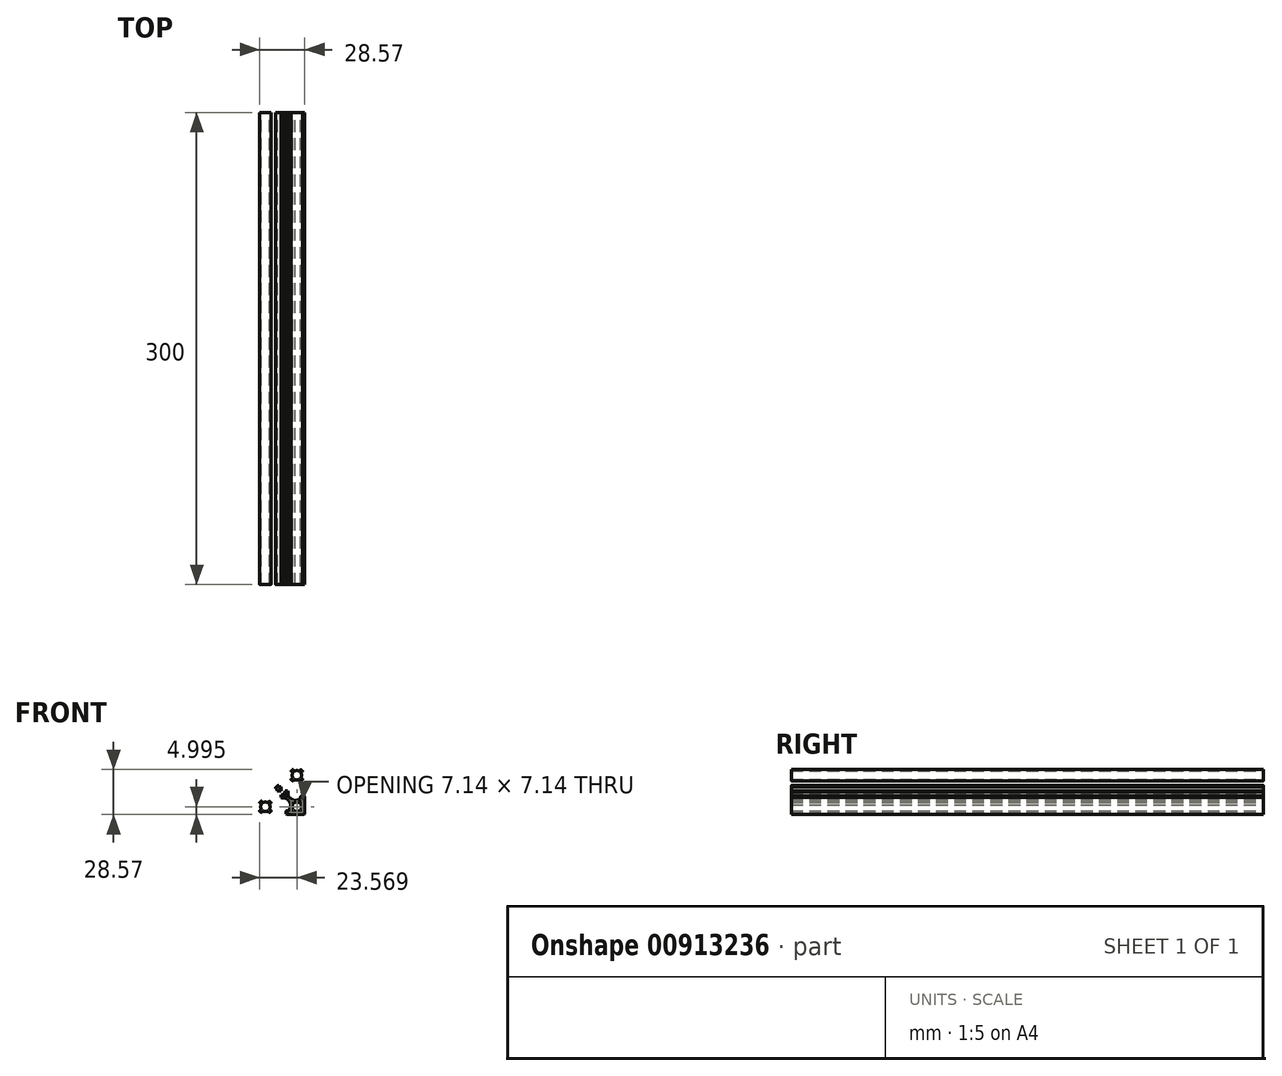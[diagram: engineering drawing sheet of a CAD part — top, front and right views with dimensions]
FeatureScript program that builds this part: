
annotation { "Feature Type Name" : "Feature", "Feature Type Description" : "" }
export const myFeature = defineFeature(function(context is Context, id is Id, definition is map)
    precondition{}
    {
        {
            var Q0;
            Q0=qCreatedBy(makeId("Front.planeOp"),FACE);
            var sketch = newSketch(context, id + "F0", { "sketchPlane" : qUnion([Q0])});
            skLineSegment(sketch, "E0", {"start": v(-2.82, -20.25) * mm, "end": v(-2.82, -15.85) * mm});
            skLineSegment(sketch, "E1", {"start": v(-5.02, -18.05) * mm, "end": v(-0.62, -18.05) * mm});
            skArc(sketch, "E2", {"start": v(-5.5, -19.39) * mm, "mid": v(-5.48, -19.57) * mm, "end": v(-5.56, -19.74) * mm});
            skLineSegment(sketch, "E3", {"start": v(-5.56, -19.74) * mm, "end": v(-6.3, -20.48) * mm});
            skArc(sketch, "E4", {"start": v(-6.3, -20.48) * mm, "mid": v(-6.4, -20.67) * mm, "end": v(-6.32, -20.88) * mm});
            skArc(sketch, "E5", {"start": v(-6.32, -20.88) * mm, "mid": v(-6, -21.24) * mm, "end": v(-5.64, -21.56) * mm});
            skArc(sketch, "E6", {"start": v(-5.64, -21.56) * mm, "mid": v(-5.44, -21.62) * mm, "end": v(-5.24, -21.54) * mm});
            skLineSegment(sketch, "E7", {"start": v(-5.24, -21.54) * mm, "end": v(-4.5, -20.8) * mm});
            skArc(sketch, "E8", {"start": v(-4.5, -20.8) * mm, "mid": v(-4.34, -20.71) * mm, "end": v(-4.16, -20.74) * mm});
            skArc(sketch, "E9", {"start": v(-4.16, -20.74) * mm, "mid": v(-2.82, -21.05) * mm, "end": v(-1.48, -20.74) * mm});
            skArc(sketch, "E10", {"start": v(-1.48, -20.74) * mm, "mid": v(-1.3, -20.71) * mm, "end": v(-1.14, -20.8) * mm});
            skLineSegment(sketch, "E11", {"start": v(-1.14, -20.8) * mm, "end": v(-0.4, -21.54) * mm});
            skArc(sketch, "E12", {"start": v(-0.4, -21.54) * mm, "mid": v(-0.2, -21.62) * mm, "end": v(0, -21.56) * mm});
            skArc(sketch, "E13", {"start": v(0, -21.56) * mm, "mid": v(0.36, -21.24) * mm, "end": v(0.68, -20.88) * mm});
            skArc(sketch, "E14", {"start": v(0.68, -20.88) * mm, "mid": v(0.75, -20.67) * mm, "end": v(0.66, -20.48) * mm});
            skLineSegment(sketch, "E15", {"start": v(0.66, -20.48) * mm, "end": v(-0.08, -19.74) * mm});
            skArc(sketch, "E16", {"start": v(-0.08, -19.74) * mm, "mid": v(-0.16, -19.57) * mm, "end": v(-0.13, -19.39) * mm});
            skArc(sketch, "E17", {"start": v(-0.13, -19.39) * mm, "mid": v(0.18, -18.05) * mm, "end": v(-0.13, -16.72) * mm});
            skArc(sketch, "E18", {"start": v(-0.13, -16.72) * mm, "mid": v(-0.16, -16.54) * mm, "end": v(-0.08, -16.37) * mm});
            skLineSegment(sketch, "E19", {"start": v(-0.08, -16.37) * mm, "end": v(0.66, -15.63) * mm});
            skArc(sketch, "E20", {"start": v(0.66, -15.63) * mm, "mid": v(0.75, -15.44) * mm, "end": v(0.68, -15.23) * mm});
            skArc(sketch, "E21", {"start": v(0.68, -15.23) * mm, "mid": v(0.36, -14.87) * mm, "end": v(0, -14.55) * mm});
            skArc(sketch, "E22", {"start": v(0, -14.55) * mm, "mid": v(-0.2, -14.48) * mm, "end": v(-0.4, -14.57) * mm});
            skLineSegment(sketch, "E23", {"start": v(-0.4, -14.57) * mm, "end": v(-1.14, -15.31) * mm});
            skArc(sketch, "E24", {"start": v(-1.14, -15.31) * mm, "mid": v(-1.3, -15.4) * mm, "end": v(-1.48, -15.37) * mm});
            skArc(sketch, "E25", {"start": v(-1.48, -15.37) * mm, "mid": v(-2.82, -15.05) * mm, "end": v(-4.16, -15.37) * mm});
            skArc(sketch, "E26", {"start": v(-4.16, -15.37) * mm, "mid": v(-4.34, -15.4) * mm, "end": v(-4.5, -15.31) * mm});
            skLineSegment(sketch, "E27", {"start": v(-4.5, -15.31) * mm, "end": v(-5.24, -14.57) * mm});
            skArc(sketch, "E28", {"start": v(-5.24, -14.57) * mm, "mid": v(-5.44, -14.48) * mm, "end": v(-5.64, -14.55) * mm});
            skArc(sketch, "E29", {"start": v(-5.64, -14.55) * mm, "mid": v(-6, -14.87) * mm, "end": v(-6.32, -15.23) * mm});
            skArc(sketch, "E30", {"start": v(-6.32, -15.23) * mm, "mid": v(-6.4, -15.44) * mm, "end": v(-6.3, -15.63) * mm});
            skLineSegment(sketch, "E31", {"start": v(-6.3, -15.63) * mm, "end": v(-5.56, -16.37) * mm});
            skArc(sketch, "E32", {"start": v(-5.56, -16.37) * mm, "mid": v(-5.48, -16.54) * mm, "end": v(-5.5, -16.72) * mm});
            skArc(sketch, "E33", {"start": v(-5.5, -16.72) * mm, "mid": v(-5.82, -18.05) * mm, "end": v(-5.5, -19.39) * mm});
            skLineSegment(sketch, "E34", {"start": v(-5.02, -38.05) * mm, "end": v(-0.62, -38.05) * mm});
            skLineSegment(sketch, "E35", {"start": v(-2.82, -35.85) * mm, "end": v(-2.82, -40.25) * mm});
            skArc(sketch, "E36", {"start": v(-5.5, -36.72) * mm, "mid": v(-5.48, -36.54) * mm, "end": v(-5.56, -36.37) * mm});
            skLineSegment(sketch, "E37", {"start": v(-5.56, -36.37) * mm, "end": v(-6.3, -35.63) * mm});
            skArc(sketch, "E38", {"start": v(-6.3, -35.63) * mm, "mid": v(-6.4, -35.44) * mm, "end": v(-6.33, -35.23) * mm});
            skArc(sketch, "E39", {"start": v(-6.33, -35.23) * mm, "mid": v(-6, -34.87) * mm, "end": v(-5.64, -34.55) * mm});
            skArc(sketch, "E40", {"start": v(-5.64, -34.55) * mm, "mid": v(-5.44, -34.48) * mm, "end": v(-5.24, -34.57) * mm});
            skLineSegment(sketch, "E41", {"start": v(-5.24, -34.57) * mm, "end": v(-4.5, -35.31) * mm});
            skArc(sketch, "E42", {"start": v(-4.5, -35.31) * mm, "mid": v(-4.34, -35.4) * mm, "end": v(-4.16, -35.37) * mm});
            skArc(sketch, "E43", {"start": v(-4.16, -35.37) * mm, "mid": v(-2.82, -35.05) * mm, "end": v(-1.48, -35.37) * mm});
            skArc(sketch, "E44", {"start": v(-1.48, -35.37) * mm, "mid": v(-1.3, -35.4) * mm, "end": v(-1.14, -35.31) * mm});
            skLineSegment(sketch, "E45", {"start": v(-1.14, -35.31) * mm, "end": v(-0.4, -34.57) * mm});
            skArc(sketch, "E46", {"start": v(-0.4, -34.57) * mm, "mid": v(-0.2, -34.48) * mm, "end": v(0, -34.55) * mm});
            skArc(sketch, "E47", {"start": v(0, -34.55) * mm, "mid": v(0.36, -34.87) * mm, "end": v(0.68, -35.23) * mm});
            skArc(sketch, "E48", {"start": v(0.68, -35.23) * mm, "mid": v(0.75, -35.44) * mm, "end": v(0.66, -35.63) * mm});
            skLineSegment(sketch, "E49", {"start": v(0.66, -35.63) * mm, "end": v(-0.08, -36.37) * mm});
            skArc(sketch, "E50", {"start": v(-0.08, -36.37) * mm, "mid": v(-0.16, -36.54) * mm, "end": v(-0.13, -36.72) * mm});
            skArc(sketch, "E51", {"start": v(-0.13, -36.72) * mm, "mid": v(0.18, -38.05) * mm, "end": v(-0.14, -39.4) * mm});
            skArc(sketch, "E52", {"start": v(-0.14, -39.4) * mm, "mid": v(-0.16, -39.57) * mm, "end": v(-0.08, -39.74) * mm});
            skLineSegment(sketch, "E53", {"start": v(-0.08, -39.74) * mm, "end": v(0.66, -40.48) * mm});
            skArc(sketch, "E54", {"start": v(0.66, -40.48) * mm, "mid": v(0.75, -40.67) * mm, "end": v(0.68, -40.88) * mm});
            skArc(sketch, "E55", {"start": v(0.68, -40.88) * mm, "mid": v(0.36, -41.24) * mm, "end": v(0, -41.56) * mm});
            skArc(sketch, "E56", {"start": v(0, -41.56) * mm, "mid": v(-0.2, -41.63) * mm, "end": v(-0.4, -41.54) * mm});
            skLineSegment(sketch, "E57", {"start": v(-0.4, -41.54) * mm, "end": v(-1.14, -40.8) * mm});
            skArc(sketch, "E58", {"start": v(-1.14, -40.8) * mm, "mid": v(-1.3, -40.71) * mm, "end": v(-1.49, -40.74) * mm});
            skArc(sketch, "E59", {"start": v(-1.49, -40.74) * mm, "mid": v(-2.82, -41.05) * mm, "end": v(-4.16, -40.74) * mm});
            skArc(sketch, "E60", {"start": v(-4.16, -40.74) * mm, "mid": v(-4.34, -40.71) * mm, "end": v(-4.5, -40.8) * mm});
            skLineSegment(sketch, "E61", {"start": v(-4.5, -40.8) * mm, "end": v(-5.24, -41.54) * mm});
            skArc(sketch, "E62", {"start": v(-5.24, -41.54) * mm, "mid": v(-5.44, -41.62) * mm, "end": v(-5.64, -41.56) * mm});
            skArc(sketch, "E63", {"start": v(-5.64, -41.56) * mm, "mid": v(-6, -41.24) * mm, "end": v(-6.33, -40.88) * mm});
            skArc(sketch, "E64", {"start": v(-6.33, -40.88) * mm, "mid": v(-6.4, -40.67) * mm, "end": v(-6.3, -40.48) * mm});
            skLineSegment(sketch, "E65", {"start": v(-6.3, -40.48) * mm, "end": v(-5.56, -39.74) * mm});
            skArc(sketch, "E66", {"start": v(-5.56, -39.74) * mm, "mid": v(-5.48, -39.57) * mm, "end": v(-5.5, -39.4) * mm});
            skArc(sketch, "E67", {"start": v(-5.5, -39.4) * mm, "mid": v(-5.82, -38.05) * mm, "end": v(-5.5, -36.72) * mm});
            skArc(sketch, "E68", {"start": v(-20.13, -36.72) * mm, "mid": v(-20.16, -36.54) * mm, "end": v(-20.07, -36.37) * mm});
            skLineSegment(sketch, "E69", {"start": v(-20.07, -36.37) * mm, "end": v(-19.33, -35.63) * mm});
            skArc(sketch, "E70", {"start": v(-19.33, -35.63) * mm, "mid": v(-19.25, -35.44) * mm, "end": v(-19.31, -35.23) * mm});
            skArc(sketch, "E71", {"start": v(-19.31, -35.23) * mm, "mid": v(-19.64, -34.87) * mm, "end": v(-20, -34.55) * mm});
            skArc(sketch, "E72", {"start": v(-20, -34.55) * mm, "mid": v(-20.2, -34.48) * mm, "end": v(-20.4, -34.57) * mm});
            skLineSegment(sketch, "E73", {"start": v(-20.4, -34.57) * mm, "end": v(-21.14, -35.31) * mm});
            skArc(sketch, "E74", {"start": v(-21.14, -35.31) * mm, "mid": v(-21.3, -35.4) * mm, "end": v(-21.48, -35.37) * mm});
            skArc(sketch, "E75", {"start": v(-21.48, -35.37) * mm, "mid": v(-22.82, -35.05) * mm, "end": v(-24.15, -35.37) * mm});
            skArc(sketch, "E76", {"start": v(-24.15, -35.37) * mm, "mid": v(-24.34, -35.4) * mm, "end": v(-24.5, -35.31) * mm});
            skLineSegment(sketch, "E77", {"start": v(-24.5, -35.31) * mm, "end": v(-25.24, -34.57) * mm});
            skArc(sketch, "E78", {"start": v(-25.24, -34.57) * mm, "mid": v(-25.44, -34.48) * mm, "end": v(-25.64, -34.55) * mm});
            skArc(sketch, "E79", {"start": v(-25.64, -34.55) * mm, "mid": v(-26, -34.87) * mm, "end": v(-26.32, -35.23) * mm});
            skArc(sketch, "E80", {"start": v(-26.32, -35.23) * mm, "mid": v(-26.39, -35.44) * mm, "end": v(-26.3, -35.63) * mm});
            skLineSegment(sketch, "E81", {"start": v(-26.3, -35.63) * mm, "end": v(-25.56, -36.37) * mm});
            skArc(sketch, "E82", {"start": v(-25.56, -36.37) * mm, "mid": v(-25.48, -36.54) * mm, "end": v(-25.5, -36.72) * mm});
            skArc(sketch, "E83", {"start": v(-25.5, -36.72) * mm, "mid": v(-25.82, -38.05) * mm, "end": v(-25.5, -39.4) * mm});
            skArc(sketch, "E84", {"start": v(-25.5, -39.4) * mm, "mid": v(-25.48, -39.57) * mm, "end": v(-25.56, -39.74) * mm});
            skLineSegment(sketch, "E85", {"start": v(-25.56, -39.74) * mm, "end": v(-26.3, -40.48) * mm});
            skArc(sketch, "E86", {"start": v(-26.3, -40.48) * mm, "mid": v(-26.39, -40.67) * mm, "end": v(-26.32, -40.88) * mm});
            skArc(sketch, "E87", {"start": v(-26.32, -40.88) * mm, "mid": v(-26, -41.24) * mm, "end": v(-25.64, -41.56) * mm});
            skArc(sketch, "E88", {"start": v(-25.64, -41.56) * mm, "mid": v(-25.44, -41.63) * mm, "end": v(-25.24, -41.54) * mm});
            skLineSegment(sketch, "E89", {"start": v(-25.24, -41.54) * mm, "end": v(-24.5, -40.8) * mm});
            skArc(sketch, "E90", {"start": v(-24.5, -40.8) * mm, "mid": v(-24.33, -40.71) * mm, "end": v(-24.15, -40.74) * mm});
            skArc(sketch, "E91", {"start": v(-24.15, -40.74) * mm, "mid": v(-22.82, -41.05) * mm, "end": v(-21.48, -40.74) * mm});
            skArc(sketch, "E92", {"start": v(-21.48, -40.74) * mm, "mid": v(-21.3, -40.71) * mm, "end": v(-21.14, -40.8) * mm});
            skLineSegment(sketch, "E93", {"start": v(-21.14, -40.8) * mm, "end": v(-20.4, -41.54) * mm});
            skArc(sketch, "E94", {"start": v(-20.4, -41.54) * mm, "mid": v(-20.2, -41.62) * mm, "end": v(-20, -41.56) * mm});
            skArc(sketch, "E95", {"start": v(-20, -41.56) * mm, "mid": v(-19.63, -41.24) * mm, "end": v(-19.31, -40.88) * mm});
            skArc(sketch, "E96", {"start": v(-19.31, -40.88) * mm, "mid": v(-19.25, -40.67) * mm, "end": v(-19.33, -40.48) * mm});
            skLineSegment(sketch, "E97", {"start": v(-19.33, -40.48) * mm, "end": v(-20.07, -39.74) * mm});
            skArc(sketch, "E98", {"start": v(-20.07, -39.74) * mm, "mid": v(-20.16, -39.57) * mm, "end": v(-20.13, -39.4) * mm});
            skArc(sketch, "E99", {"start": v(-20.13, -39.4) * mm, "mid": v(-19.82, -38.05) * mm, "end": v(-20.13, -36.72) * mm});
            skLineSegment(sketch, "E100", {"start": v(-22.82, -35.85) * mm, "end": v(-22.82, -40.25) * mm});
            skLineSegment(sketch, "E101", {"start": v(-20.62, -38.05) * mm, "end": v(-25.02, -38.05) * mm});
            skLineSegment(sketch, "E102", {"start": v(-20.62, -18.05) * mm, "end": v(-25.02, -18.05) * mm});
            skLineSegment(sketch, "E103", {"start": v(-22.82, -20.25) * mm, "end": v(-22.82, -15.85) * mm});
            skLineSegment(sketch, "E104", {"start": v(2.64, -28.05) * mm, "end": v(-29.04, -28.05) * mm});
            skLineSegment(sketch, "E105", {"start": v(-12.82, -44) * mm, "end": v(-12.82, -12.06) * mm});
            skArc(sketch, "E106", {"start": v(-9.58, -26.47) * mm, "mid": v(-9.36, -26.3) * mm, "end": v(-9.38, -26.02) * mm});
            skArc(sketch, "E107", {"start": v(-9.38, -26.02) * mm, "mid": v(-10, -25.23) * mm, "end": v(-10.78, -24.61) * mm});
            skArc(sketch, "E108", {"start": v(-10.78, -24.61) * mm, "mid": v(-11.06, -24.6) * mm, "end": v(-11.23, -24.82) * mm});
            skLineSegment(sketch, "E109", {"start": v(-11.23, -24.82) * mm, "end": v(-11.37, -25.56) * mm});
            skArc(sketch, "E110", {"start": v(-11.37, -25.56) * mm, "mid": v(-11.52, -25.77) * mm, "end": v(-11.78, -25.78) * mm});
            skArc(sketch, "E111", {"start": v(-11.78, -25.78) * mm, "mid": v(-12.82, -25.55) * mm, "end": v(-13.85, -25.78) * mm});
            skArc(sketch, "E112", {"start": v(-13.85, -25.78) * mm, "mid": v(-14.11, -25.77) * mm, "end": v(-14.27, -25.56) * mm});
            skLineSegment(sketch, "E113", {"start": v(-14.27, -25.56) * mm, "end": v(-14.4, -24.82) * mm});
            skArc(sketch, "E114", {"start": v(-14.4, -24.82) * mm, "mid": v(-14.57, -24.6) * mm, "end": v(-14.85, -24.61) * mm});
            skArc(sketch, "E115", {"start": v(-14.85, -24.61) * mm, "mid": v(-15.65, -25.23) * mm, "end": v(-16.26, -26.02) * mm});
            skArc(sketch, "E116", {"start": v(-16.26, -26.02) * mm, "mid": v(-16.27, -26.3) * mm, "end": v(-16.06, -26.47) * mm});
            skLineSegment(sketch, "E117", {"start": v(-16.06, -26.47) * mm, "end": v(-15.31, -26.6) * mm});
            skArc(sketch, "E118", {"start": v(-15.31, -26.6) * mm, "mid": v(-15.1, -26.76) * mm, "end": v(-15.1, -27.02) * mm});
            skArc(sketch, "E119", {"start": v(-15.1, -27.02) * mm, "mid": v(-15.32, -28.05) * mm, "end": v(-15.1, -29.09) * mm});
            skArc(sketch, "E120", {"start": v(-15.1, -29.09) * mm, "mid": v(-15.1, -29.35) * mm, "end": v(-15.31, -29.5) * mm});
            skLineSegment(sketch, "E121", {"start": v(-15.31, -29.5) * mm, "end": v(-16.06, -29.64) * mm});
            skArc(sketch, "E122", {"start": v(-16.06, -29.64) * mm, "mid": v(-16.27, -29.81) * mm, "end": v(-16.26, -30.09) * mm});
            skArc(sketch, "E123", {"start": v(-16.26, -30.09) * mm, "mid": v(-15.65, -30.88) * mm, "end": v(-14.85, -31.5) * mm});
            skArc(sketch, "E124", {"start": v(-14.85, -31.5) * mm, "mid": v(-14.57, -31.51) * mm, "end": v(-14.4, -31.3) * mm});
            skLineSegment(sketch, "E125", {"start": v(-14.4, -31.3) * mm, "end": v(-14.27, -30.55) * mm});
            skArc(sketch, "E126", {"start": v(-14.27, -30.55) * mm, "mid": v(-14.11, -30.34) * mm, "end": v(-13.85, -30.33) * mm});
            skArc(sketch, "E127", {"start": v(-13.85, -30.33) * mm, "mid": v(-12.82, -30.55) * mm, "end": v(-11.78, -30.33) * mm});
            skArc(sketch, "E128", {"start": v(-11.78, -30.33) * mm, "mid": v(-11.52, -30.34) * mm, "end": v(-11.37, -30.55) * mm});
            skLineSegment(sketch, "E129", {"start": v(-11.37, -30.55) * mm, "end": v(-11.23, -31.3) * mm});
            skArc(sketch, "E130", {"start": v(-11.23, -31.3) * mm, "mid": v(-11.06, -31.51) * mm, "end": v(-10.78, -31.5) * mm});
            skArc(sketch, "E131", {"start": v(-10.78, -31.5) * mm, "mid": v(-10, -30.88) * mm, "end": v(-9.38, -30.09) * mm});
            skArc(sketch, "E132", {"start": v(-9.38, -30.09) * mm, "mid": v(-9.36, -29.81) * mm, "end": v(-9.58, -29.64) * mm});
            skLineSegment(sketch, "E133", {"start": v(-9.58, -29.64) * mm, "end": v(-10.32, -29.5) * mm});
            skArc(sketch, "E134", {"start": v(-10.32, -29.5) * mm, "mid": v(-10.53, -29.35) * mm, "end": v(-10.54, -29.09) * mm});
            skArc(sketch, "E135", {"start": v(-10.54, -29.09) * mm, "mid": v(-10.32, -28.05) * mm, "end": v(-10.54, -27.02) * mm});
            skArc(sketch, "E136", {"start": v(-10.54, -27.02) * mm, "mid": v(-10.53, -26.76) * mm, "end": v(-10.32, -26.6) * mm});
            skLineSegment(sketch, "E137", {"start": v(-10.32, -26.6) * mm, "end": v(-9.58, -26.47) * mm});
            skArc(sketch, "E138", {"start": v(-20.13, -19.39) * mm, "mid": v(-20.16, -19.57) * mm, "end": v(-20.08, -19.74) * mm});
            skLineSegment(sketch, "E139", {"start": v(-20.08, -19.74) * mm, "end": v(-19.33, -20.48) * mm});
            skArc(sketch, "E140", {"start": v(-19.33, -20.48) * mm, "mid": v(-19.25, -20.67) * mm, "end": v(-19.31, -20.88) * mm});
            skArc(sketch, "E141", {"start": v(-19.31, -20.88) * mm, "mid": v(-19.64, -21.24) * mm, "end": v(-20, -21.56) * mm});
            skArc(sketch, "E142", {"start": v(-20, -21.56) * mm, "mid": v(-20.2, -21.62) * mm, "end": v(-20.4, -21.54) * mm});
            skLineSegment(sketch, "E143", {"start": v(-20.4, -21.54) * mm, "end": v(-21.14, -20.8) * mm});
            skArc(sketch, "E144", {"start": v(-21.14, -20.8) * mm, "mid": v(-21.3, -20.71) * mm, "end": v(-21.48, -20.74) * mm});
            skArc(sketch, "E145", {"start": v(-21.48, -20.74) * mm, "mid": v(-22.82, -21.05) * mm, "end": v(-24.15, -20.74) * mm});
            skArc(sketch, "E146", {"start": v(-24.15, -20.74) * mm, "mid": v(-24.34, -20.71) * mm, "end": v(-24.5, -20.8) * mm});
            skLineSegment(sketch, "E147", {"start": v(-24.5, -20.8) * mm, "end": v(-25.24, -21.54) * mm});
            skArc(sketch, "E148", {"start": v(-25.24, -21.54) * mm, "mid": v(-25.44, -21.62) * mm, "end": v(-25.64, -21.56) * mm});
            skArc(sketch, "E149", {"start": v(-25.64, -21.56) * mm, "mid": v(-26, -21.24) * mm, "end": v(-26.32, -20.88) * mm});
            skArc(sketch, "E150", {"start": v(-26.32, -20.88) * mm, "mid": v(-26.39, -20.67) * mm, "end": v(-26.3, -20.48) * mm});
            skLineSegment(sketch, "E151", {"start": v(-26.3, -20.48) * mm, "end": v(-25.56, -19.74) * mm});
            skArc(sketch, "E152", {"start": v(-25.56, -19.74) * mm, "mid": v(-25.48, -19.57) * mm, "end": v(-25.5, -19.39) * mm});
            skArc(sketch, "E153", {"start": v(-25.5, -19.39) * mm, "mid": v(-25.82, -18.05) * mm, "end": v(-25.5, -16.72) * mm});
            skArc(sketch, "E154", {"start": v(-25.5, -16.72) * mm, "mid": v(-25.48, -16.54) * mm, "end": v(-25.56, -16.37) * mm});
            skLineSegment(sketch, "E155", {"start": v(-25.56, -16.37) * mm, "end": v(-26.3, -15.63) * mm});
            skArc(sketch, "E156", {"start": v(-26.3, -15.63) * mm, "mid": v(-26.39, -15.44) * mm, "end": v(-26.32, -15.23) * mm});
            skArc(sketch, "E157", {"start": v(-26.32, -15.23) * mm, "mid": v(-26, -14.87) * mm, "end": v(-25.64, -14.55) * mm});
            skArc(sketch, "E158", {"start": v(-25.64, -14.55) * mm, "mid": v(-25.44, -14.48) * mm, "end": v(-25.24, -14.57) * mm});
            skLineSegment(sketch, "E159", {"start": v(-25.24, -14.57) * mm, "end": v(-24.5, -15.31) * mm});
            skArc(sketch, "E160", {"start": v(-24.5, -15.31) * mm, "mid": v(-24.34, -15.4) * mm, "end": v(-24.15, -15.37) * mm});
            skArc(sketch, "E161", {"start": v(-24.15, -15.37) * mm, "mid": v(-22.82, -15.05) * mm, "end": v(-21.48, -15.37) * mm});
            skArc(sketch, "E162", {"start": v(-21.48, -15.37) * mm, "mid": v(-21.3, -15.4) * mm, "end": v(-21.14, -15.31) * mm});
            skLineSegment(sketch, "E163", {"start": v(-21.14, -15.31) * mm, "end": v(-20.4, -14.57) * mm});
            skArc(sketch, "E164", {"start": v(-20.4, -14.57) * mm, "mid": v(-20.2, -14.48) * mm, "end": v(-20, -14.55) * mm});
            skArc(sketch, "E165", {"start": v(-20, -14.55) * mm, "mid": v(-19.64, -14.87) * mm, "end": v(-19.31, -15.23) * mm});
            skArc(sketch, "E166", {"start": v(-19.31, -15.23) * mm, "mid": v(-19.25, -15.44) * mm, "end": v(-19.33, -15.63) * mm});
            skLineSegment(sketch, "E167", {"start": v(-19.33, -15.63) * mm, "end": v(-20.08, -16.37) * mm});
            skArc(sketch, "E168", {"start": v(-20.08, -16.37) * mm, "mid": v(-20.16, -16.54) * mm, "end": v(-20.13, -16.72) * mm});
            skArc(sketch, "E169", {"start": v(-20.13, -16.72) * mm, "mid": v(-19.82, -18.05) * mm, "end": v(-20.13, -19.39) * mm});
            skLineSegment(sketch, "E170", {"start": v(-8.87, -43.05) * mm, "end": v(-9.67, -42.55) * mm});
            skLineSegment(sketch, "E171", {"start": v(-9.67, -42.55) * mm, "end": v(-9.67, -40.85) * mm});
            skArc(sketch, "E172", {"start": v(-9.67, -40.85) * mm, "mid": v(-9.58, -40.64) * mm, "end": v(-9.37, -40.55) * mm});
            skLineSegment(sketch, "E173", {"start": v(-9.37, -40.55) * mm, "end": v(-7.72, -40.55) * mm});
            skLineSegment(sketch, "E174", {"start": v(-7.72, -40.55) * mm, "end": v(-6.73, -37.5) * mm});
            skArc(sketch, "E175", {"start": v(-6.73, -37.5) * mm, "mid": v(-6.68, -37.24) * mm, "end": v(-6.7, -36.98) * mm});
            skArc(sketch, "E176", {"start": v(-6.7, -36.98) * mm, "mid": v(-7.54, -34.94) * mm, "end": v(-8.81, -33.14) * mm});
            skArc(sketch, "E177", {"start": v(-8.81, -33.14) * mm, "mid": v(-9.66, -32.7) * mm, "end": v(-10.6, -32.55) * mm});
            skLineSegment(sketch, "E178", {"start": v(-10.6, -32.55) * mm, "end": v(-12.32, -32.55) * mm});
            skLineSegment(sketch, "E179", {"start": v(-12.32, -32.55) * mm, "end": v(-12.82, -32.05) * mm});
            skLineSegment(sketch, "E180", {"start": v(-12.82, -32.05) * mm, "end": v(-13.32, -32.55) * mm});
            skLineSegment(sketch, "E181", {"start": v(-13.32, -32.55) * mm, "end": v(-15.04, -32.55) * mm});
            skArc(sketch, "E182", {"start": v(-15.04, -32.55) * mm, "mid": v(-15.98, -32.7) * mm, "end": v(-16.82, -33.14) * mm});
            skArc(sketch, "E183", {"start": v(-16.82, -33.14) * mm, "mid": v(-18.1, -34.94) * mm, "end": v(-18.93, -36.98) * mm});
            skArc(sketch, "E184", {"start": v(-18.93, -36.98) * mm, "mid": v(-18.95, -37.24) * mm, "end": v(-18.9, -37.5) * mm});
            skLineSegment(sketch, "E185", {"start": v(-18.9, -37.5) * mm, "end": v(-17.92, -40.55) * mm});
            skLineSegment(sketch, "E186", {"start": v(-17.92, -40.55) * mm, "end": v(-16.27, -40.55) * mm});
            skArc(sketch, "E187", {"start": v(-16.27, -40.55) * mm, "mid": v(-16.06, -40.64) * mm, "end": v(-15.97, -40.85) * mm});
            skLineSegment(sketch, "E188", {"start": v(-15.97, -40.85) * mm, "end": v(-15.97, -42.55) * mm});
            skLineSegment(sketch, "E189", {"start": v(-15.97, -42.55) * mm, "end": v(-16.77, -43.05) * mm});
            skLineSegment(sketch, "E190", {"start": v(-16.77, -43.05) * mm, "end": v(-26.82, -43.05) * mm});
            skArc(sketch, "E191", {"start": v(-26.82, -43.05) * mm, "mid": v(-27.52, -42.76) * mm, "end": v(-27.82, -42.05) * mm});
            skLineSegment(sketch, "E192", {"start": v(-27.82, -42.05) * mm, "end": v(-27.82, -32) * mm});
            skLineSegment(sketch, "E193", {"start": v(-27.82, -32) * mm, "end": v(-27.32, -31.2) * mm});
            skLineSegment(sketch, "E194", {"start": v(-27.32, -31.2) * mm, "end": v(-25.62, -31.2) * mm});
            skArc(sketch, "E195", {"start": v(-25.62, -31.2) * mm, "mid": v(-25.4, -31.3) * mm, "end": v(-25.32, -31.5) * mm});
            skLineSegment(sketch, "E196", {"start": v(-25.32, -31.5) * mm, "end": v(-25.32, -33.15) * mm});
            skLineSegment(sketch, "E197", {"start": v(-25.32, -33.15) * mm, "end": v(-22.27, -34.14) * mm});
            skArc(sketch, "E198", {"start": v(-22.27, -34.14) * mm, "mid": v(-22, -34.19) * mm, "end": v(-21.75, -34.17) * mm});
            skArc(sketch, "E199", {"start": v(-21.75, -34.17) * mm, "mid": v(-19.7, -33.33) * mm, "end": v(-17.9, -32.06) * mm});
            skArc(sketch, "E200", {"start": v(-17.9, -32.06) * mm, "mid": v(-17.47, -31.21) * mm, "end": v(-17.32, -30.27) * mm});
            skLineSegment(sketch, "E201", {"start": v(-17.32, -30.27) * mm, "end": v(-17.32, -28.55) * mm});
            skLineSegment(sketch, "E202", {"start": v(-17.32, -28.55) * mm, "end": v(-16.82, -28.05) * mm});
            skLineSegment(sketch, "E203", {"start": v(-16.82, -28.05) * mm, "end": v(-17.32, -27.55) * mm});
            skLineSegment(sketch, "E204", {"start": v(-17.32, -27.55) * mm, "end": v(-17.32, -25.84) * mm});
            skArc(sketch, "E205", {"start": v(-17.32, -25.84) * mm, "mid": v(-17.47, -24.9) * mm, "end": v(-17.9, -24.05) * mm});
            skArc(sketch, "E206", {"start": v(-17.9, -24.05) * mm, "mid": v(-19.7, -22.78) * mm, "end": v(-21.75, -21.94) * mm});
            skArc(sketch, "E207", {"start": v(-21.75, -21.94) * mm, "mid": v(-22, -21.92) * mm, "end": v(-22.27, -21.97) * mm});
            skLineSegment(sketch, "E208", {"start": v(-22.27, -21.97) * mm, "end": v(-25.32, -22.95) * mm});
            skLineSegment(sketch, "E209", {"start": v(-25.32, -22.95) * mm, "end": v(-25.32, -24.6) * mm});
            skArc(sketch, "E210", {"start": v(-25.32, -24.6) * mm, "mid": v(-25.4, -24.82) * mm, "end": v(-25.62, -24.9) * mm});
            skLineSegment(sketch, "E211", {"start": v(-25.62, -24.9) * mm, "end": v(-27.32, -24.9) * mm});
            skLineSegment(sketch, "E212", {"start": v(-27.32, -24.9) * mm, "end": v(-27.82, -24.1) * mm});
            skLineSegment(sketch, "E213", {"start": v(-27.82, -24.1) * mm, "end": v(-27.82, -14.05) * mm});
            skArc(sketch, "E214", {"start": v(-27.82, -14.05) * mm, "mid": v(-27.52, -13.35) * mm, "end": v(-26.82, -13.05) * mm});
            skLineSegment(sketch, "E215", {"start": v(-26.82, -13.05) * mm, "end": v(-16.77, -13.05) * mm});
            skLineSegment(sketch, "E216", {"start": v(-16.77, -13.05) * mm, "end": v(-15.97, -13.55) * mm});
            skLineSegment(sketch, "E217", {"start": v(-15.97, -13.55) * mm, "end": v(-15.97, -15.25) * mm});
            skArc(sketch, "E218", {"start": v(-15.97, -15.25) * mm, "mid": v(-16.06, -15.47) * mm, "end": v(-16.27, -15.55) * mm});
            skLineSegment(sketch, "E219", {"start": v(-16.27, -15.55) * mm, "end": v(-17.92, -15.55) * mm});
            skLineSegment(sketch, "E220", {"start": v(-17.92, -15.55) * mm, "end": v(-18.9, -18.6) * mm});
            skArc(sketch, "E221", {"start": v(-18.9, -18.6) * mm, "mid": v(-18.95, -18.86) * mm, "end": v(-18.93, -19.13) * mm});
            skArc(sketch, "E222", {"start": v(-18.93, -19.13) * mm, "mid": v(-18.1, -21.16) * mm, "end": v(-16.82, -22.96) * mm});
            skArc(sketch, "E223", {"start": v(-16.82, -22.96) * mm, "mid": v(-15.98, -23.4) * mm, "end": v(-15.04, -23.55) * mm});
            skLineSegment(sketch, "E224", {"start": v(-15.04, -23.55) * mm, "end": v(-13.32, -23.55) * mm});
            skLineSegment(sketch, "E225", {"start": v(-13.32, -23.55) * mm, "end": v(-12.82, -24.05) * mm});
            skLineSegment(sketch, "E226", {"start": v(-12.82, -24.05) * mm, "end": v(-12.32, -23.55) * mm});
            skLineSegment(sketch, "E227", {"start": v(-12.32, -23.55) * mm, "end": v(-10.6, -23.55) * mm});
            skArc(sketch, "E228", {"start": v(-10.6, -23.55) * mm, "mid": v(-9.66, -23.4) * mm, "end": v(-8.81, -22.96) * mm});
            skArc(sketch, "E229", {"start": v(-8.81, -22.96) * mm, "mid": v(-7.54, -21.16) * mm, "end": v(-6.7, -19.13) * mm});
            skArc(sketch, "E230", {"start": v(-6.7, -19.13) * mm, "mid": v(-6.68, -18.86) * mm, "end": v(-6.73, -18.6) * mm});
            skLineSegment(sketch, "E231", {"start": v(-6.73, -18.6) * mm, "end": v(-7.72, -15.55) * mm});
            skLineSegment(sketch, "E232", {"start": v(-7.72, -15.55) * mm, "end": v(-9.37, -15.55) * mm});
            skArc(sketch, "E233", {"start": v(-9.37, -15.55) * mm, "mid": v(-9.58, -15.47) * mm, "end": v(-9.67, -15.25) * mm});
            skLineSegment(sketch, "E234", {"start": v(-9.67, -15.25) * mm, "end": v(-9.67, -13.55) * mm});
            skLineSegment(sketch, "E235", {"start": v(-9.67, -13.55) * mm, "end": v(-8.87, -13.05) * mm});
            skLineSegment(sketch, "E236", {"start": v(-8.87, -13.05) * mm, "end": v(1.18, -13.05) * mm});
            skArc(sketch, "E237", {"start": v(1.18, -13.05) * mm, "mid": v(1.89, -13.35) * mm, "end": v(2.18, -14.05) * mm});
            skLineSegment(sketch, "E238", {"start": v(2.18, -14.05) * mm, "end": v(2.18, -24.1) * mm});
            skLineSegment(sketch, "E239", {"start": v(2.18, -24.1) * mm, "end": v(1.68, -24.9) * mm});
            skLineSegment(sketch, "E240", {"start": v(1.68, -24.9) * mm, "end": v(-0.02, -24.9) * mm});
            skArc(sketch, "E241", {"start": v(-0.02, -24.9) * mm, "mid": v(-0.23, -24.82) * mm, "end": v(-0.32, -24.6) * mm});
            skLineSegment(sketch, "E242", {"start": v(-0.32, -24.6) * mm, "end": v(-0.32, -22.95) * mm});
            skLineSegment(sketch, "E243", {"start": v(-0.32, -22.95) * mm, "end": v(-3.37, -21.97) * mm});
            skArc(sketch, "E244", {"start": v(-3.37, -21.97) * mm, "mid": v(-3.63, -21.92) * mm, "end": v(-3.9, -21.94) * mm});
            skArc(sketch, "E245", {"start": v(-3.9, -21.94) * mm, "mid": v(-5.93, -22.78) * mm, "end": v(-7.73, -24.05) * mm});
            skArc(sketch, "E246", {"start": v(-7.73, -24.05) * mm, "mid": v(-8.17, -24.9) * mm, "end": v(-8.32, -25.84) * mm});
            skLineSegment(sketch, "E247", {"start": v(-8.32, -25.84) * mm, "end": v(-8.32, -27.55) * mm});
            skLineSegment(sketch, "E248", {"start": v(-8.32, -27.55) * mm, "end": v(-8.82, -28.05) * mm});
            skLineSegment(sketch, "E249", {"start": v(-8.82, -28.05) * mm, "end": v(-8.32, -28.55) * mm});
            skLineSegment(sketch, "E250", {"start": v(-8.32, -28.55) * mm, "end": v(-8.32, -30.27) * mm});
            skArc(sketch, "E251", {"start": v(-8.32, -30.27) * mm, "mid": v(-8.17, -31.21) * mm, "end": v(-7.73, -32.06) * mm});
            skArc(sketch, "E252", {"start": v(-7.73, -32.06) * mm, "mid": v(-5.93, -33.33) * mm, "end": v(-3.9, -34.17) * mm});
            skArc(sketch, "E253", {"start": v(-3.9, -34.17) * mm, "mid": v(-3.63, -34.19) * mm, "end": v(-3.37, -34.14) * mm});
            skLineSegment(sketch, "E254", {"start": v(-3.37, -34.14) * mm, "end": v(-0.32, -33.15) * mm});
            skLineSegment(sketch, "E255", {"start": v(-0.32, -33.15) * mm, "end": v(-0.32, -31.5) * mm});
            skArc(sketch, "E256", {"start": v(-0.32, -31.5) * mm, "mid": v(-0.23, -31.3) * mm, "end": v(-0.02, -31.2) * mm});
            skLineSegment(sketch, "E257", {"start": v(-0.02, -31.2) * mm, "end": v(1.68, -31.2) * mm});
            skLineSegment(sketch, "E258", {"start": v(1.68, -31.2) * mm, "end": v(2.18, -32) * mm});
            skLineSegment(sketch, "E259", {"start": v(2.18, -32) * mm, "end": v(2.18, -42.05) * mm});
            skArc(sketch, "E260", {"start": v(2.18, -42.05) * mm, "mid": v(1.89, -42.76) * mm, "end": v(1.18, -43.05) * mm});
            skLineSegment(sketch, "E261", {"start": v(1.18, -43.05) * mm, "end": v(-8.87, -43.05) * mm});
            skSolve(sketch);
        }
        {
            var Q0;
            Q0=makeQuery(id+"F0.imprint","IMPRINT",FACE,{"disambiguationData":[TD([[makeQuery(id+"F0.imprint","IMPRINT",EDGE,{"derivedFrom":sQuery(id+"F0.wireOp",EDGE,"E2")}),-1.0]])]});
            var Q1;
            {var subQ1=sQuery(id+"F0.wireOp",EDGE,"E112");Q1=makeQuery(id+"F0.imprint","IMPRINT",FACE,{"disambiguationData":[TD([[makeQuery(id+"F0.imprint","IMPRINT",EDGE,{"derivedFrom":subQ1}),-1.0]])]});}
            var Q2;
            Q2=makeQuery(id+"F0.imprint","IMPRINT",FACE,{"disambiguationData":[TD([[makeQuery(id+"F0.imprint","IMPRINT",EDGE,{"derivedFrom":sQuery(id+"F0.wireOp",EDGE,"E36")}),1.0]])]});
            var Q3;
            Q3=makeQuery(id+"F0.imprint","IMPRINT",FACE,{"disambiguationData":[TD([[makeQuery(id+"F0.imprint","IMPRINT",EDGE,{"derivedFrom":sQuery(id+"F0.wireOp",EDGE,"E68")}),-1.0]])]});
            extrude(context, id + "F1", {"entities" : qUnion([Q0, Q1, Q2, Q3]), "depth" : 300 * mm, "offsetDistance" : 25 * mm});
        }
    });
